SOLIDWORKS PART (.sldprt)
format: sldprt  version: not decoded by parser v0  size: 152,064 bytes
history: native  units: mm
features: sketch x6, extrude x2, cut_extrude x2, material x1, hole x1, fillet x1 (+13 scaffold rows collapsed; 3 parser-record rows omitted)
feature tree (29):
  scaffold x13  (default folders/planes/origin — collapsed)
  material  "Material <not specified>"
  parser-record x3  (decoder bookkeeping rows leaked as tree rows — omitted from the tree; the rows remain in map.json)
  sketch  "Sketch1"  dims[D1=16.2052mm D2=25.4mm]
  extrude  "Base-Extrude"  Depth=3.6322mm
  sketch  "Sketch2"  dims[D1=8.9916mm D2=7.112mm]
  extrude  "Boss-Extrude1"  Depth=2.032mm
  hole  "5/16-18 Tapped Hole1"  Diameter=6.5278mm Depth=5.6642mm
  sketch  "3DSketch1"
  sketch  "Sketch3"  dims[hole-wizard template sketch: 41 standard entries collapsed; hole parameters kept: c12.Thru Tap Drill Dia.=6.5278mm c12.Thru Tap Drill Depth=5.6642mm c12.Thread Dia.=7.9375mm c12.Thread Depth=15.875mm]
  sketch  "Sketch4"  dims[D1=3.429mm]
  cut_extrude  "Cut-Extrude1"  [1 undecoded]
  sketch  "Sketch6"  dims[D1=3.429mm]
  cut_extrude  "Cut-Extrude2"  [1 undecoded]
  fillet  "Fillet1"  Radius=0.508mm
decode coverage: 9 of 12 modeling features carry decoded parameters
note: ~ marks probable driven/reference dimensions
note: 2 parameter values undecoded
note: suppression state not decoded; provenance and decode notes live in map.json
